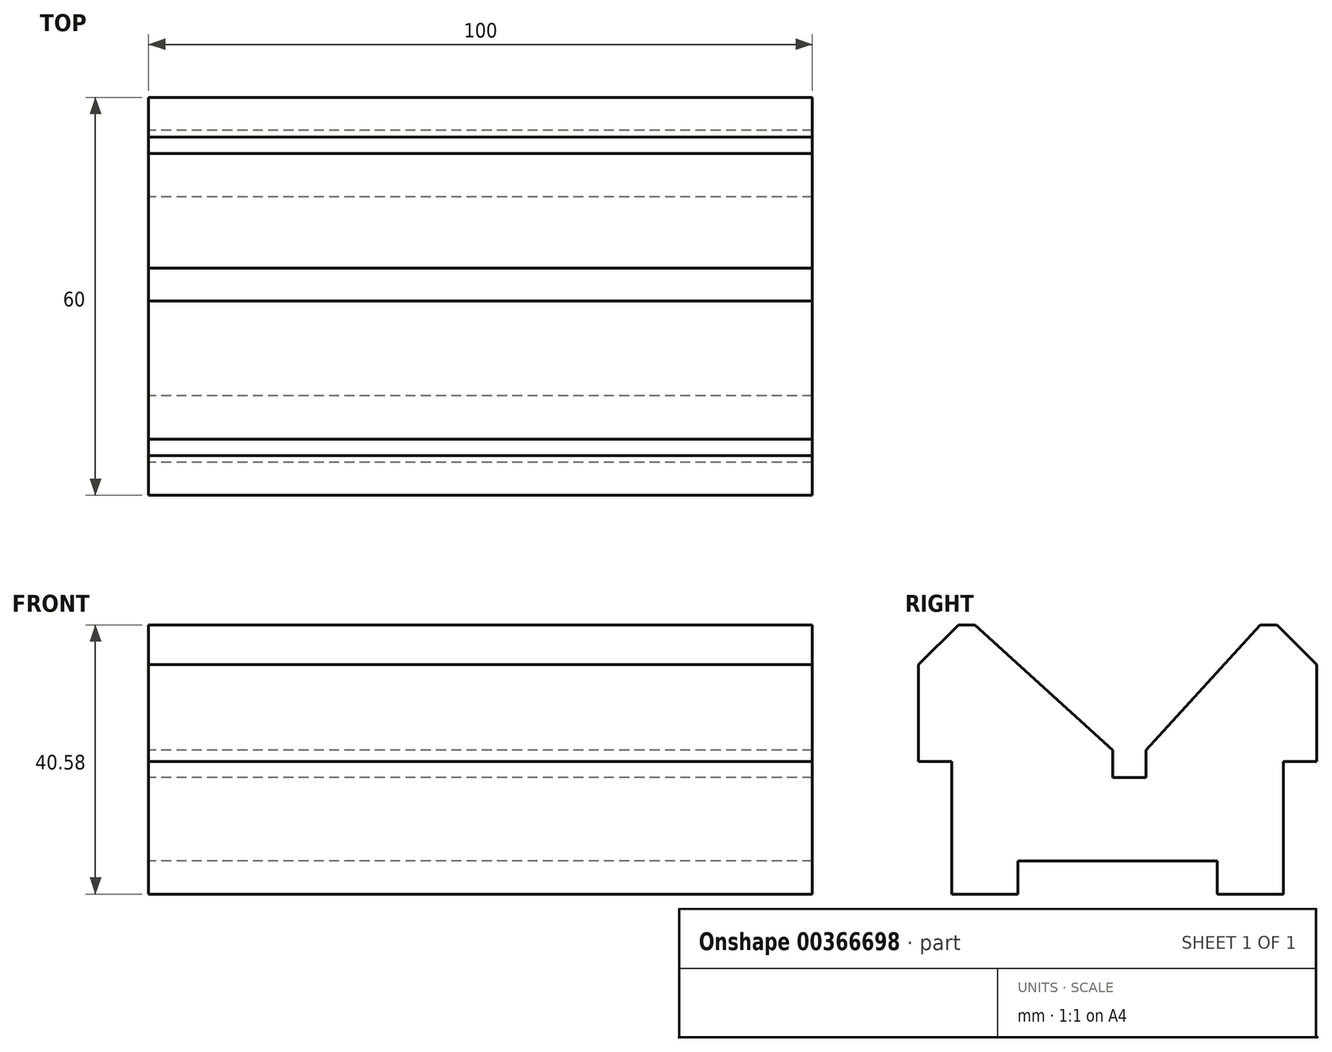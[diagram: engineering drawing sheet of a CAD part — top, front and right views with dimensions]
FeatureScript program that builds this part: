
annotation { "Feature Type Name" : "Feature", "Feature Type Description" : "" }
export const myFeature = defineFeature(function(context is Context, id is Id, definition is map)
    precondition{}
    {
        {
            var Q0;
            Q0=qCreatedBy(makeId("Right.planeOp"),FACE);
            var sketch = newSketch(context, id + "F0", { "sketchPlane" : qUnion([Q0])});
            skLineSegment(sketch, "E0", {"start": v(0, 20) * mm, "end": v(0, 34.58) * mm});
            skLineSegment(sketch, "E1", {"start": v(0, 34.58) * mm, "end": v(6, 40.58) * mm});
            skLineSegment(sketch, "E2", {"start": v(6, 40.58) * mm, "end": v(8.5, 40.58) * mm});
            skLineSegment(sketch, "E3", {"start": v(8.5, 40.58) * mm, "end": v(29.28, 21.66) * mm});
            skLineSegment(sketch, "E4", {"start": v(29.28, 21.66) * mm, "end": v(29.28, 17.58) * mm});
            skLineSegment(sketch, "E5", {"start": v(29.28, 17.58) * mm, "end": v(34.28, 17.58) * mm});
            skLineSegment(sketch, "E6", {"start": v(34.28, 17.58) * mm, "end": v(34.28, 21.66) * mm});
            skLineSegment(sketch, "E7", {"start": v(60, 34.58) * mm, "end": v(60, 20) * mm});
            skLineSegment(sketch, "E8", {"start": v(60, 20) * mm, "end": v(55, 20) * mm});
            skLineSegment(sketch, "E9", {"start": v(55, 20) * mm, "end": v(55, 0) * mm});
            skLineSegment(sketch, "E10", {"start": v(55, 0) * mm, "end": v(45, 0) * mm});
            skLineSegment(sketch, "E11", {"start": v(45, 0) * mm, "end": v(45, 5) * mm});
            skLineSegment(sketch, "E12", {"start": v(45, 5) * mm, "end": v(15, 5) * mm});
            skLineSegment(sketch, "E13", {"start": v(15, 5) * mm, "end": v(15, 0) * mm});
            skLineSegment(sketch, "E14", {"start": v(15, 0) * mm, "end": v(5, 0) * mm});
            skLineSegment(sketch, "E15", {"start": v(5, 0) * mm, "end": v(5, 20) * mm});
            skLineSegment(sketch, "E16", {"start": v(5, 20) * mm, "end": v(0, 20) * mm});
            skPoint(sketch, "E17.end.orphan", {"position": v(51.5, 40.58) * mm});
            skPoint(sketch, "E17.start.orphan", {"position": v(54, 40.58) * mm});
            skLineSegment(sketch, "E18", {"start": v(54, 40.58) * mm, "end": v(60, 34.58) * mm});
            skLineSegment(sketch, "E19", {"start": v(54, 40.58) * mm, "end": v(51.5, 40.58) * mm});
            skLineSegment(sketch, "E20", {"start": v(34.28, 21.66) * mm, "end": v(51.5, 40.58) * mm});
            skSolve(sketch);
        }
        {
            var Q0;
            Q0=makeQuery(id+"F0.imprint","IMPRINT",FACE,{"disambiguationData":[TD([[makeQuery(id+"F0.imprint","IMPRINT",EDGE,{"derivedFrom":sQuery(id+"F0.wireOp",EDGE,"E0")}),-1.0]])]});
            extrude(context, id + "F1", {"entities" : qUnion([Q0]), "depth" : 100 * mm});
        }
    });
